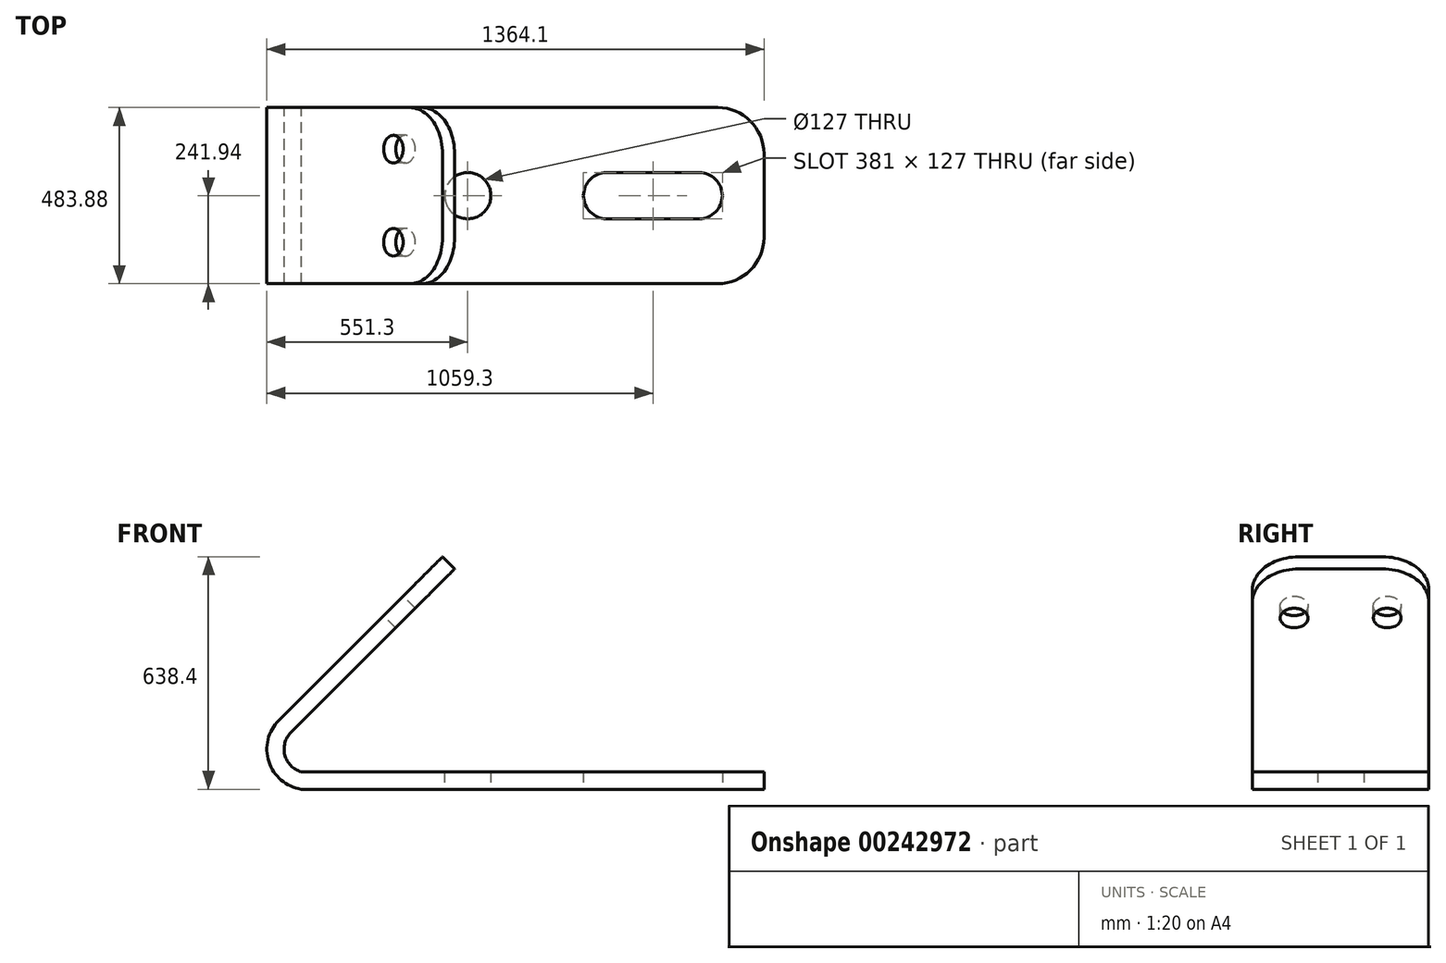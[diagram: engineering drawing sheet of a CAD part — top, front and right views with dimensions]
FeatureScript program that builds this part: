
annotation { "Feature Type Name" : "Feature", "Feature Type Description" : "" }
export const myFeature = defineFeature(function(context is Context, id is Id, definition is map)
    precondition{}
    {
        {
            var Q0;
            Q0=qCreatedBy(makeId("Front.planeOp"),FACE);
            var sketch = newSketch(context, id + "F0", { "sketchPlane" : qUnion([Q0])});
            skLineSegment(sketch, "E0.bottom", {"start": v(0, 0) * mm, "end": v(1270, 0) * mm});
            skLineSegment(sketch, "E0.top", {"start": v(0, 48.26) * mm, "end": v(1270, 48.26) * mm});
            skLineSegment(sketch, "E0.left", {"start": v(0, 0) * mm, "end": v(0, 48.26) * mm});
            skLineSegment(sketch, "E0.right", {"start": v(1270, 0) * mm, "end": v(1270, 48.26) * mm});
            skLineSegment(sketch, "E1", {"start": v(1270, 24.13) * mm, "end": v(-99.6, 24.13) * mm, "construction": true});
            skArc(sketch, "E2", {"start": v(0, 48.26) * mm, "mid": v(-44.83, 94.12) * mm, "end": v(-28, 156) * mm});
            skArc(sketch, "E3", {"start": v(0, 0) * mm, "mid": v(-88.66, 75.9) * mm, "end": v(-61.37, 189.38) * mm});
            skLineSegment(sketch, "E4", {"start": v(-28, 156) * mm, "end": v(421.02, 605.02) * mm});
            skLineSegment(sketch, "E5", {"start": v(-61.37, 189.38) * mm, "end": v(387.64, 638.4) * mm});
            skLineSegment(sketch, "E6", {"start": v(387.64, 638.4) * mm, "end": v(421.02, 605.02) * mm});
            skSolve(sketch);
        }
        {
            var Q0;
            Q0=qSketchRegion(id+"F0",true);
            extrude(context, id + "F1", {"entities" : qUnion([Q0]), "endBound" : BoundingType.SYMMETRIC, "depth" : 483.87 * mm});
        }
        {
            var Q0;
            Q0=makeQuery(id+"F1.opExtrude","SWEPT_FACE",FACE,{"disambiguationData":[OSD([sQuery(id+"F0.wireOp",EDGE,"E0.bottom")])]});
            var sketch = newSketch(context, id + "F2", { "sketchPlane" : qUnion([Q0])});
            skLineSegment(sketch, "E7", {"start": v(0, 0) * mm, "end": v(1270, 0) * mm, "construction": true});
            skLineSegment(sketch, "E8", {"start": v(1270, 0) * mm, "end": v(1155.7, 0) * mm});
            skArc(sketch, "E9", {"start": v(1155.7, 0) * mm, "mid": v(1137.1, 44.9) * mm, "end": v(1092.2, 63.5) * mm});
            skArc(sketch, "E10", {"start": v(1155.7, 0) * mm, "mid": v(1137.1, -44.9) * mm, "end": v(1092.2, -63.5) * mm});
            skLineSegment(sketch, "E11", {"start": v(1092.2, 63.5) * mm, "end": v(838.2, 63.5) * mm});
            skLineSegment(sketch, "E12", {"start": v(838.2, -63.5) * mm, "end": v(1092.2, -63.5) * mm});
            skArc(sketch, "E13", {"start": v(838.2, -63.5) * mm, "mid": v(793.3, -44.9) * mm, "end": v(774.7, 0) * mm});
            skArc(sketch, "E14", {"start": v(774.7, 0) * mm, "mid": v(793.3, 44.9) * mm, "end": v(838.2, 63.5) * mm});
            skSolve(sketch);
        }
        {
            var Q0;
            Q0=qSketchRegion(id+"F2",true);
            extrude(context, id + "F3", {"entities" : qUnion([Q0]), "operationType" : NewBodyOperationType.REMOVE, "oppositeDirection" : true, "depth" : 254 * mm});
        }
        {
            var Q0;
            Q0=makeQuery(id+"F1.opExtrude","SWEPT_FACE",FACE,{"disambiguationData":[OSD([sQuery(id+"F0.wireOp",EDGE,"E0.bottom")])]});
            var sketch = newSketch(context, id + "F4", { "sketchPlane" : qUnion([Q0])});
            skLineSegment(sketch, "E15", {"start": v(1270, 241.94) * mm, "end": v(457.2, 241.94) * mm});
            skLineSegment(sketch, "E16", {"start": v(457.2, 241.94) * mm, "end": v(457.2, 0) * mm});
            skCircle(sketch, "E17", {"center": v(457.2, 0) * mm, "radius": 63.5 * mm});
            skSolve(sketch);
        }
        {
            var Q0;
            Q0=makeQuery(id+"F4.imprint","IMPRINT",FACE,{"disambiguationData":[TD([[makeQuery(id+"F4.imprint","IMPRINT",EDGE,{"derivedFrom":sQuery(id+"F4.wireOp",EDGE,"E17")}),1.0]])]});
            extrude(context, id + "F5", {"entities" : qUnion([Q0]), "operationType" : NewBodyOperationType.REMOVE, "oppositeDirection" : true, "depth" : 127 * mm});
        }
        {
            var Q0;
            Q0=makeQuery(id+"F1.opExtrude","SWEPT_FACE",FACE,{"disambiguationData":[OSD([sQuery(id+"F0.wireOp",EDGE,"E5")])]});
            var sketch = newSketch(context, id + "F6", { "sketchPlane" : qUnion([Q0])});
            skLineSegment(sketch, "E18", {"start": v(-241.94, 90.52) * mm, "end": v(-127.76, 90.52) * mm});
            skLineSegment(sketch, "E19", {"start": v(-127.76, 725.52) * mm, "end": v(-127.76, 535.02) * mm});
            skLineSegment(sketch, "E20", {"start": v(0, 725.52) * mm, "end": v(0, -259.8) * mm, "construction": true});
            skPoint(sketch, "E20.endSnap0", {"position": v(0, 725.52) * mm});
            skCircle(sketch, "E21", {"center": v(-127.76, 535.02) * mm, "radius": 38.1 * mm});
            skCircle(sketch, "E22.MirrorC", {"center": v(127.76, 535.02) * mm, "radius": 38.1 * mm});
            skSolve(sketch);
        }
        {
            var Q0;
            Q0=qSketchRegion(id+"F6",true);
            extrude(context, id + "F7", {"entities" : qUnion([Q0]), "operationType" : NewBodyOperationType.REMOVE, "oppositeDirection" : true, "depth" : 101.6 * mm});
        }
        {
            var Q0;
            Q0=makeQuery(id+"F1.opExtrude","CAP_EDGE",EDGE,{"disambiguationData":[OSD([sQuery(id+"F0.wireOp",EDGE,"E6")])],"isStart":true});
            var Q1;
            Q1=makeQuery(id+"F1.opExtrude","CAP_EDGE",EDGE,{"disambiguationData":[OSD([sQuery(id+"F0.wireOp",EDGE,"E6")])],"isStart":false});
            var Q2;
            Q2=makeQuery(id+"F1.opExtrude","CAP_EDGE",EDGE,{"disambiguationData":[OSD([sQuery(id+"F0.wireOp",EDGE,"E0.right")])],"isStart":false});
            var Q3;
            Q3=makeQuery(id+"F1.opExtrude","CAP_EDGE",EDGE,{"disambiguationData":[OSD([sQuery(id+"F0.wireOp",EDGE,"E0.right")])],"isStart":true});
            fillet(context, id + "F8", {"entities" : qUnion([Q0, Q1, Q2, Q3]), "radius" : 127 * mm, "tangentPropagation" : true, "allowEdgeOverflow" : false});
        }
    });
